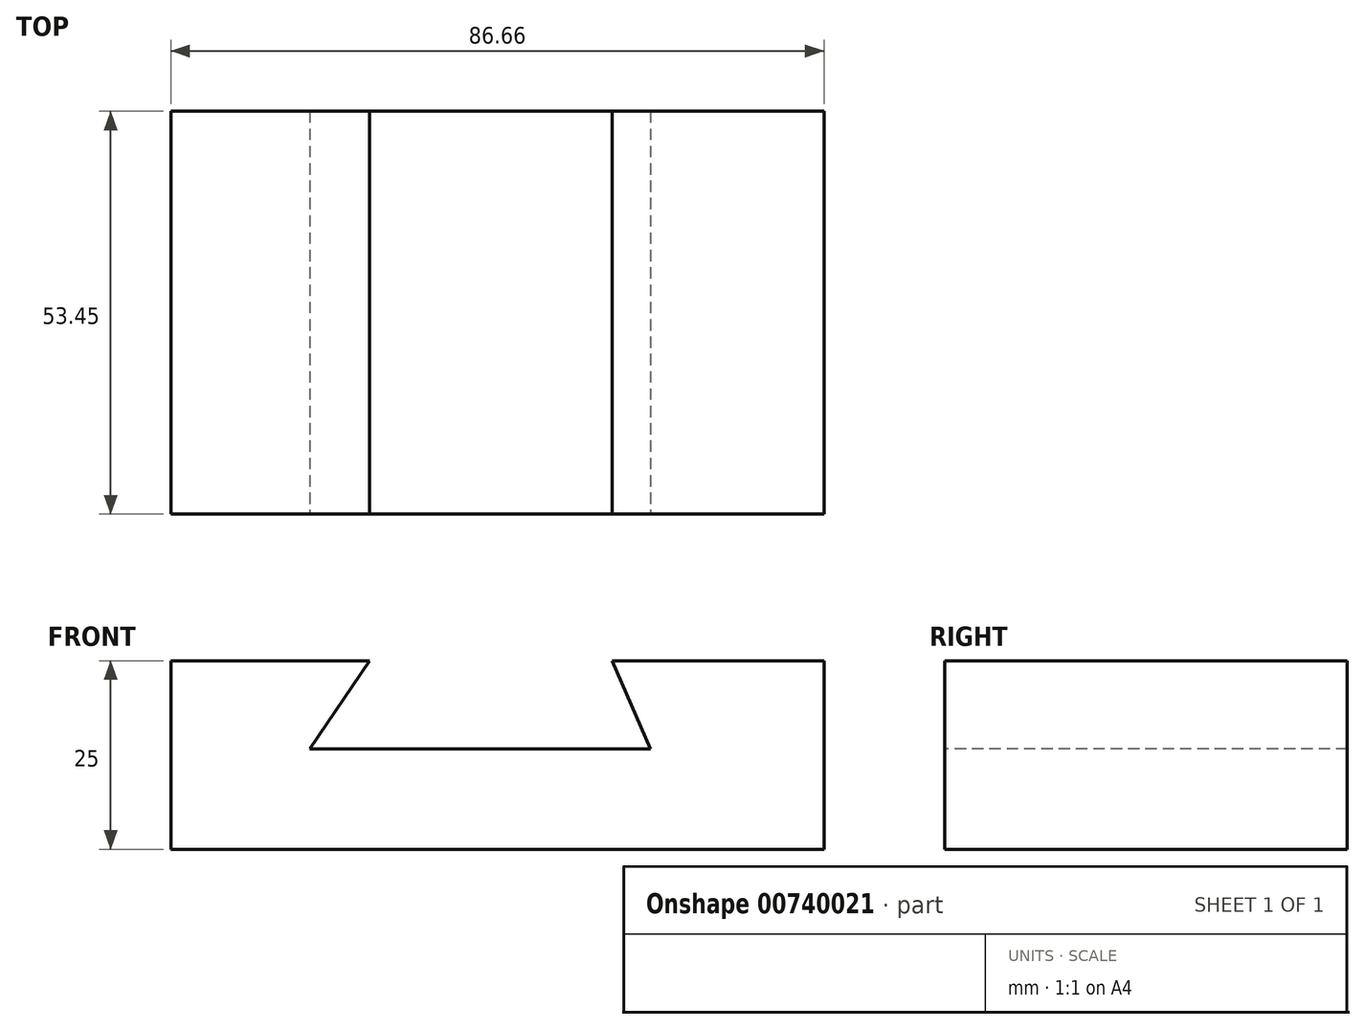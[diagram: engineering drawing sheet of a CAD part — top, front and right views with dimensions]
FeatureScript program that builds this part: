
annotation { "Feature Type Name" : "Feature", "Feature Type Description" : "" }
export const myFeature = defineFeature(function(context is Context, id is Id, definition is map)
    precondition{}
    {
        {
            var Q0;
            Q0=qCreatedBy(makeId("Top.planeOp"),FACE);
            var sketch = newSketch(context, id + "F0", { "sketchPlane" : qUnion([Q0])});
            skLineSegment(sketch, "E0.bottom", {"start": v(-37.16, 32.42) * mm, "end": v(49.5, 32.42) * mm});
            skLineSegment(sketch, "E0.top", {"start": v(-37.16, -21.03) * mm, "end": v(49.5, -21.03) * mm});
            skLineSegment(sketch, "E0.left", {"start": v(-37.16, 32.42) * mm, "end": v(-37.16, -21.03) * mm});
            skLineSegment(sketch, "E0.right", {"start": v(49.5, 32.42) * mm, "end": v(49.5, -21.03) * mm});
            skSolve(sketch);
        }
        {
            var Q0;
            Q0 = qSketchRegion(id + "F0", true);
            extrude(context, id + "F1", {"entities" : qUnion([Q0]), "depth" : 25 * mm, "offsetDistance" : 25 * mm});
        }
        {
            var Q0;
            Q0=makeQuery(id+"F1.opExtrude","SWEPT_FACE",FACE,{"disambiguationData":[OSD([sQuery(id+"F0.wireOp",EDGE,"E0.top")])]});
            var sketch = newSketch(context, id + "F2", { "sketchPlane" : qUnion([Q0])});
            skLineSegment(sketch, "E1", {"start": v(-10.8, 25) * mm, "end": v(-18.74, 13.34) * mm});
            skLineSegment(sketch, "E2", {"start": v(-18.74, 13.34) * mm, "end": v(26.44, 13.34) * mm});
            skLineSegment(sketch, "E3", {"start": v(26.44, 13.34) * mm, "end": v(21.4, 25) * mm});
            skSolve(sketch);
        }
        {
            var Q0;
            {var subQ0=sQuery(id+"F2.wireOp",EDGE,"E1");Q0=makeQuery(id+"F2.imprint","IMPRINT",FACE,{"disambiguationData":[TD([[makeQuery(id+"F2.imprint","IMPRINT",EDGE,{"derivedFrom":subQ0}),1.0]])]});}
            extrude(context, id + "F3", {"entities" : qUnion([Q0]), "operationType" : NewBodyOperationType.REMOVE, "oppositeDirection" : true, "depth" : 2000 * mm, "offsetDistance" : 25 * mm});
        }
    });
